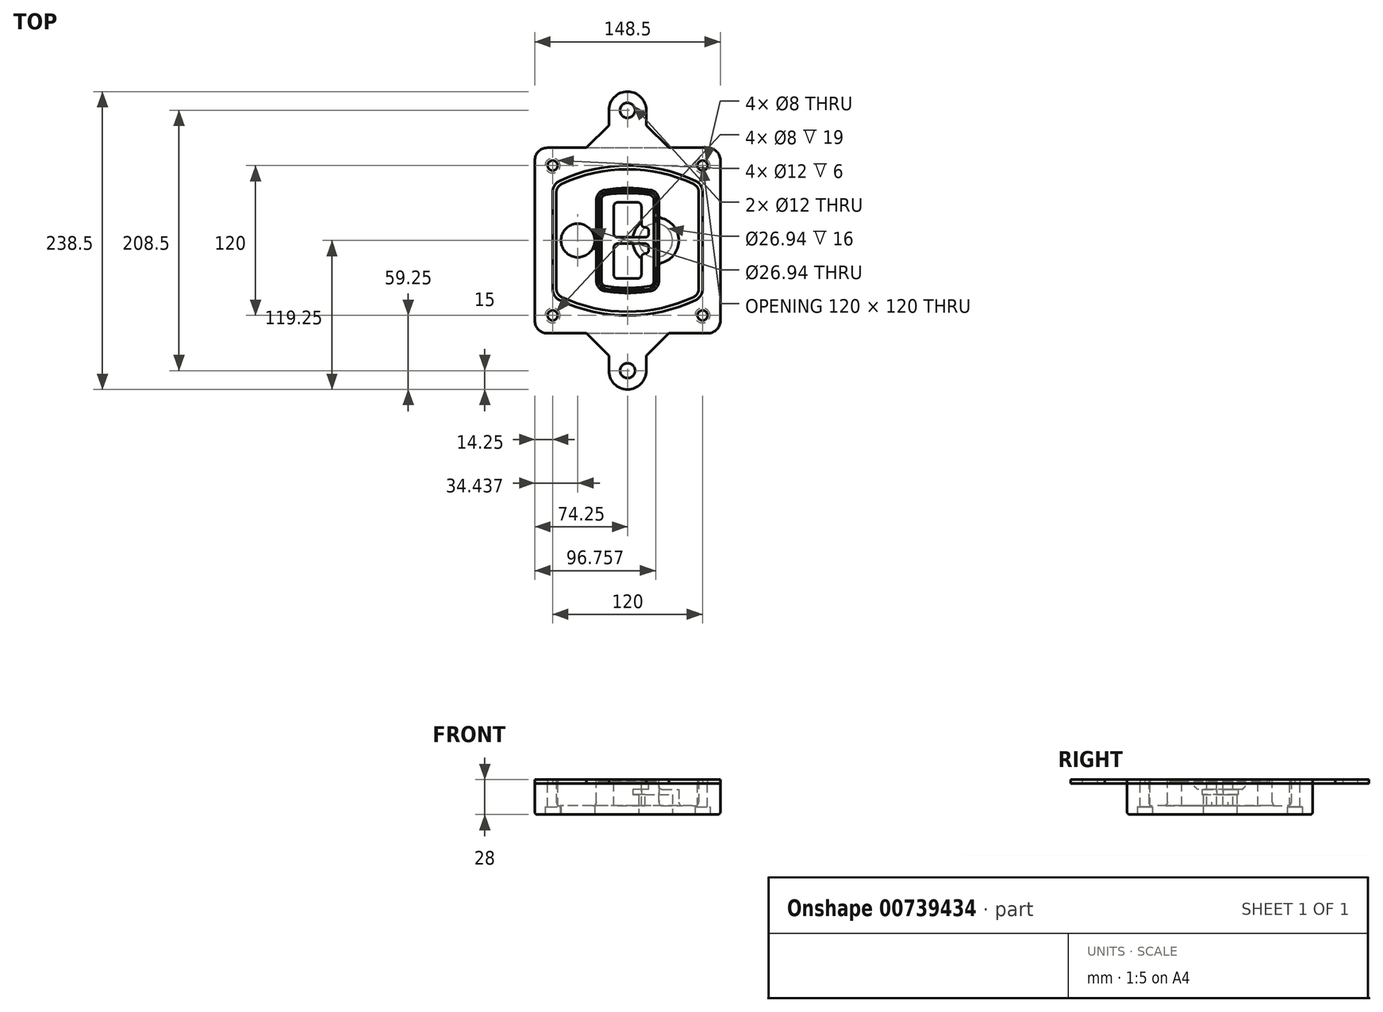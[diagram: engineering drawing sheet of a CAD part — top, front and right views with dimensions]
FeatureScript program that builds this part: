
annotation { "Feature Type Name" : "Feature", "Feature Type Description" : "" }
export const myFeature = defineFeature(function(context is Context, id is Id, definition is map)
    precondition{}
    {
        {
            var Q0;
            Q0=qCreatedBy(makeId("Top.planeOp"),FACE);
            var sketch = newSketch(context, id + "F0", { "sketchPlane" : qUnion([Q0])});
            skPoint(sketch, "E0.rect.middle", {"position": v(0, 0) * mm});
            skLineSegment(sketch, "E1.bottom", {"start": v(-64.25, -74.25) * mm, "end": v(64.25, -74.25) * mm});
            skLineSegment(sketch, "E1.top", {"start": v(-64.25, 74.25) * mm, "end": v(64.25, 74.25) * mm});
            skLineSegment(sketch, "E1.left", {"start": v(-74.25, -64.25) * mm, "end": v(-74.25, 64.25) * mm});
            skLineSegment(sketch, "E1.right", {"start": v(74.25, -64.25) * mm, "end": v(74.25, 64.25) * mm});
            skLineSegment(sketch, "E2", {"start": v(-74.25, 74.25) * mm, "end": v(74.25, -74.25) * mm, "construction": true});
            skLineSegment(sketch, "E3", {"start": v(74.25, 74.25) * mm, "end": v(-74.25, -74.25) * mm, "construction": true});
            skCircle(sketch, "E4", {"center": v(-60, 60) * mm, "radius": 4 * mm});
            skCircle(sketch, "E5", {"center": v(60, 60) * mm, "radius": 4 * mm});
            skCircle(sketch, "E6", {"center": v(60, -60) * mm, "radius": 4 * mm});
            skCircle(sketch, "E7", {"center": v(-60, -60) * mm, "radius": 4 * mm});
            skLineSegment(sketch, "E8", {"start": v(-60, 60) * mm, "end": v(60, 60) * mm, "construction": true});
            skLineSegment(sketch, "E9", {"start": v(60, 60) * mm, "end": v(60, -60) * mm, "construction": true});
            skLineSegment(sketch, "E10", {"start": v(60, -60) * mm, "end": v(-60, -60) * mm, "construction": true});
            skLineSegment(sketch, "E11", {"start": v(-60, -60) * mm, "end": v(-60, 60) * mm, "construction": true});
            skLineSegment(sketch, "E12", {"start": v(-60, 38.83) * mm, "end": v(-60, -38.83) * mm});
            skLineSegment(sketch, "E13", {"start": v(60, 38.83) * mm, "end": v(60, -38.83) * mm});
            skArc(sketch, "E14", {"start": v(54.26, 47.88) * mm, "mid": v(0, 60) * mm, "end": v(-54.26, 47.88) * mm});
            skArc(sketch, "E15", {"start": v(-54.26, -47.88) * mm, "mid": v(0, -60) * mm, "end": v(54.26, -47.88) * mm});
            skLineSegment(sketch, "E16", {"start": v(-60, 0) * mm, "end": v(60, 0) * mm, "construction": true});
            skPoint(sketch, "E17.visualSharp", {"position": v(-60, -45) * mm});
            skArc(sketch, "E17.filletArc", {"start": v(-60, -38.83) * mm, "mid": v(-58.44, -44.2) * mm, "end": v(-54.26, -47.88) * mm});
            skPoint(sketch, "E18.visualSharp", {"position": v(-60, 45) * mm});
            skArc(sketch, "E18.filletArc", {"start": v(-54.26, 47.88) * mm, "mid": v(-58.44, 44.2) * mm, "end": v(-60, 38.83) * mm});
            skPoint(sketch, "E19.visualSharp", {"position": v(60, 45) * mm});
            skArc(sketch, "E19.filletArc", {"start": v(60, 38.83) * mm, "mid": v(58.44, 44.2) * mm, "end": v(54.26, 47.88) * mm});
            skPoint(sketch, "E20.visualSharp", {"position": v(60, -45) * mm});
            skArc(sketch, "E20.filletArc", {"start": v(54.26, -47.88) * mm, "mid": v(58.44, -44.2) * mm, "end": v(60, -38.83) * mm});
            skPoint(sketch, "E21.visualSharp", {"position": v(-74.25, 74.25) * mm});
            skArc(sketch, "E21.filletArc", {"start": v(-64.25, 74.25) * mm, "mid": v(-71.32, 71.32) * mm, "end": v(-74.25, 64.25) * mm});
            skPoint(sketch, "E22.visualSharp", {"position": v(74.25, 74.25) * mm});
            skArc(sketch, "E22.filletArc", {"start": v(74.25, 64.25) * mm, "mid": v(71.32, 71.32) * mm, "end": v(64.25, 74.25) * mm});
            skPoint(sketch, "E23.visualSharp", {"position": v(74.25, -74.25) * mm});
            skArc(sketch, "E23.filletArc", {"start": v(64.25, -74.25) * mm, "mid": v(71.32, -71.32) * mm, "end": v(74.25, -64.25) * mm});
            skPoint(sketch, "E24.visualSharp", {"position": v(-74.25, -74.25) * mm});
            skArc(sketch, "E24.filletArc", {"start": v(-74.25, -64.25) * mm, "mid": v(-71.32, -71.32) * mm, "end": v(-64.25, -74.25) * mm});
            skArc(sketch, "E25.0", {"start": v(57, 38.83) * mm, "mid": v(55.9, 42.58) * mm, "end": v(52.98, 45.17) * mm});
            skLineSegment(sketch, "E25.1", {"start": v(57, 38.83) * mm, "end": v(57, -38.83) * mm});
            skArc(sketch, "E25.2", {"start": v(52.98, -45.17) * mm, "mid": v(55.9, -42.58) * mm, "end": v(57, -38.83) * mm});
            skArc(sketch, "E25.3", {"start": v(-52.98, -45.17) * mm, "mid": v(0, -57) * mm, "end": v(52.98, -45.17) * mm});
            skArc(sketch, "E25.4", {"start": v(-57, -38.83) * mm, "mid": v(-55.9, -42.58) * mm, "end": v(-52.98, -45.17) * mm});
            skArc(sketch, "E25.5", {"start": v(52.98, 45.17) * mm, "mid": v(0, 57) * mm, "end": v(-52.98, 45.17) * mm});
            skLineSegment(sketch, "E25.6", {"start": v(-57, 38.83) * mm, "end": v(-57, -38.83) * mm});
            skArc(sketch, "E25.7", {"start": v(-52.98, 45.17) * mm, "mid": v(-55.9, 42.58) * mm, "end": v(-57, 38.83) * mm});
            skArc(sketch, "E26.0", {"start": v(-55.96, 51.5) * mm, "mid": v(-61.82, 46.33) * mm, "end": v(-64, 38.83) * mm});
            skArc(sketch, "E26.1", {"start": v(55.96, 51.5) * mm, "mid": v(0, 64) * mm, "end": v(-55.96, 51.5) * mm});
            skArc(sketch, "E26.2", {"start": v(64, 38.83) * mm, "mid": v(61.82, 46.33) * mm, "end": v(55.96, 51.5) * mm});
            skLineSegment(sketch, "E26.3", {"start": v(64, 38.83) * mm, "end": v(64, -38.83) * mm});
            skArc(sketch, "E26.4", {"start": v(55.96, -51.5) * mm, "mid": v(61.82, -46.33) * mm, "end": v(64, -38.83) * mm});
            skLineSegment(sketch, "E26.5", {"start": v(-64, 38.83) * mm, "end": v(-64, -38.83) * mm});
            skArc(sketch, "E26.6", {"start": v(-55.96, -51.5) * mm, "mid": v(0, -64) * mm, "end": v(55.96, -51.5) * mm});
            skArc(sketch, "E26.7", {"start": v(-64, -38.83) * mm, "mid": v(-61.82, -46.33) * mm, "end": v(-55.96, -51.5) * mm});
            skSolve(sketch);
        }
        {
            var Q0;
            Q0=makeQuery(id+"F0.imprint","IMPRINT",FACE,{"disambiguationData":[TD([[makeQuery(id+"F0.imprint","IMPRINT",EDGE,{"derivedFrom":sQuery(id+"F0.wireOp",EDGE,"E1.bottom")}),1.0]])]});
            var Q1;
            Q1=makeQuery(id+"F0.imprint","IMPRINT",FACE,{"disambiguationData":[TD([[makeQuery(id+"F0.imprint","IMPRINT",EDGE,{"derivedFrom":sQuery(id+"F0.wireOp",EDGE,"E12")}),1.0]])]});
            var Q2;
            Q2=makeQuery(id+"F0.imprint","IMPRINT",FACE,{"disambiguationData":[TD([[makeQuery(id+"F0.imprint","IMPRINT",EDGE,{"derivedFrom":sQuery(id+"F0.wireOp",EDGE,"E25.0")}),1.0]])]});
            var Q3;
            Q3=makeQuery(id+"F0.imprint","IMPRINT",FACE,{"disambiguationData":[TD([[makeQuery(id+"F0.imprint","IMPRINT",EDGE,{"derivedFrom":sQuery(id+"F0.wireOp",EDGE,"E12")}),-1.0]])]});
            extrude(context, id + "F1", {"entities" : qUnion([Q0, Q1, Q2, Q3]), "oppositeDirection" : true, "depth" : 25 * mm});
        }
        {
            var Q0;
            Q0=makeQuery(id+"F0.imprint","IMPRINT",FACE,{"disambiguationData":[TD([[makeQuery(id+"F0.imprint","IMPRINT",EDGE,{"derivedFrom":sQuery(id+"F0.wireOp",EDGE,"E12")}),1.0]])]});
            extrude(context, id + "F2", {"entities" : qUnion([Q0]), "operationType" : NewBodyOperationType.ADD, "depth" : 3 * mm});
        }
        {
            var Q0;
            Q0=makeQuery(id+"F0.imprint","IMPRINT",FACE,{"disambiguationData":[TD([[makeQuery(id+"F0.imprint","IMPRINT",EDGE,{"derivedFrom":sQuery(id+"F0.wireOp",EDGE,"E25.0")}),1.0]])]});
            extrude(context, id + "F3", {"entities" : qUnion([Q0]), "operationType" : NewBodyOperationType.REMOVE, "oppositeDirection" : true, "depth" : 18 * mm});
        }
        {
            var Q0;
            Q0=makeQuery(id+"F2.opExtrude","CAP_FACE",FACE,{"disambiguationData":[OSD([sQuery(id+"F0.wireOp",EDGE,"E12"),sQuery(id+"F0.wireOp",EDGE,"E13"),sQuery(id+"F0.wireOp",EDGE,"E14"),sQuery(id+"F0.wireOp",EDGE,"E15"),sQuery(id+"F0.wireOp",EDGE,"E17.filletArc"),sQuery(id+"F0.wireOp",EDGE,"E18.filletArc"),sQuery(id+"F0.wireOp",EDGE,"E19.filletArc"),sQuery(id+"F0.wireOp",EDGE,"E20.filletArc"),sQuery(id+"F0.wireOp",EDGE,"E25.0"),sQuery(id+"F0.wireOp",EDGE,"E25.1"),sQuery(id+"F0.wireOp",EDGE,"E25.2"),sQuery(id+"F0.wireOp",EDGE,"E25.3"),sQuery(id+"F0.wireOp",EDGE,"E25.4"),sQuery(id+"F0.wireOp",EDGE,"E25.5"),sQuery(id+"F0.wireOp",EDGE,"E25.6"),sQuery(id+"F0.wireOp",EDGE,"E25.7")])],"isStart":false});
            var sketch = newSketch(context, id + "F4", { "sketchPlane" : qUnion([Q0])});
            skArc(sketch, "E27.0", {"start": v(-18.34, -40.45) * mm, "mid": v(0, -42) * mm, "end": v(18.34, -40.45) * mm});
            skArc(sketch, "E28.0", {"start": v(18.34, 40.45) * mm, "mid": v(0, 42) * mm, "end": v(-18.34, 40.45) * mm});
            skLineSegment(sketch, "E29", {"start": v(-25, 32.57) * mm, "end": v(-25, -32.57) * mm});
            skLineSegment(sketch, "E30", {"start": v(25, 32.57) * mm, "end": v(25, -32.57) * mm});
            skLineSegment(sketch, "E31", {"start": v(-25, 39.1) * mm, "end": v(25, 39.1) * mm, "construction": true});
            skLineSegment(sketch, "E32", {"start": v(-25, -39.1) * mm, "end": v(25, -39.1) * mm, "construction": true});
            skPoint(sketch, "E33.visualSharp", {"position": v(-25, 39.1) * mm});
            skArc(sketch, "E33.filletArc", {"start": v(-18.34, 40.45) * mm, "mid": v(-23.11, 37.73) * mm, "end": v(-25, 32.57) * mm});
            skPoint(sketch, "E34.visualSharp", {"position": v(25, 39.1) * mm});
            skArc(sketch, "E34.filletArc", {"start": v(25, 32.57) * mm, "mid": v(23.11, 37.73) * mm, "end": v(18.34, 40.45) * mm});
            skPoint(sketch, "E35.visualSharp", {"position": v(25, -39.1) * mm});
            skArc(sketch, "E35.filletArc", {"start": v(18.34, -40.45) * mm, "mid": v(23.11, -37.73) * mm, "end": v(25, -32.57) * mm});
            skPoint(sketch, "E36.visualSharp", {"position": v(-25, -39.1) * mm});
            skArc(sketch, "E36.filletArc", {"start": v(-25, -32.57) * mm, "mid": v(-23.11, -37.73) * mm, "end": v(-18.34, -40.45) * mm});
            skArc(sketch, "E37.0", {"start": v(52.98, 45.17) * mm, "mid": v(0, 57) * mm, "end": v(-52.98, 45.17) * mm});
            skArc(sketch, "E37.1", {"start": v(-52.98, 45.17) * mm, "mid": v(-55.9, 42.58) * mm, "end": v(-57, 38.83) * mm});
            skLineSegment(sketch, "E37.2", {"start": v(-57, 38.83) * mm, "end": v(-57, -38.83) * mm});
            skArc(sketch, "E37.3", {"start": v(-57, -38.83) * mm, "mid": v(-55.9, -42.58) * mm, "end": v(-52.98, -45.17) * mm});
            skArc(sketch, "E37.4", {"start": v(-52.98, -45.17) * mm, "mid": v(0, -57) * mm, "end": v(52.98, -45.17) * mm});
            skArc(sketch, "E37.5", {"start": v(52.98, -45.17) * mm, "mid": v(55.9, -42.58) * mm, "end": v(57, -38.83) * mm});
            skLineSegment(sketch, "E37.6", {"start": v(57, 38.83) * mm, "end": v(57, -38.83) * mm});
            skArc(sketch, "E37.7", {"start": v(57, 38.83) * mm, "mid": v(55.9, 42.58) * mm, "end": v(52.98, 45.17) * mm});
            skLineSegment(sketch, "E38.0", {"start": v(23, 32.57) * mm, "end": v(23, -32.57) * mm});
            skArc(sketch, "E38.1", {"start": v(18, -38.48) * mm, "mid": v(21.58, -36.44) * mm, "end": v(23, -32.57) * mm});
            skArc(sketch, "E38.2", {"start": v(-18, -38.48) * mm, "mid": v(0, -40) * mm, "end": v(18, -38.48) * mm});
            skArc(sketch, "E38.3", {"start": v(-23, -32.57) * mm, "mid": v(-21.58, -36.44) * mm, "end": v(-18, -38.48) * mm});
            skLineSegment(sketch, "E38.4", {"start": v(-23, 32.57) * mm, "end": v(-23, -32.57) * mm});
            skArc(sketch, "E38.5", {"start": v(23, 32.57) * mm, "mid": v(21.58, 36.44) * mm, "end": v(18, 38.48) * mm});
            skArc(sketch, "E38.6", {"start": v(-18, 38.48) * mm, "mid": v(-21.58, 36.44) * mm, "end": v(-23, 32.57) * mm});
            skArc(sketch, "E38.7", {"start": v(18, 38.48) * mm, "mid": v(0, 40) * mm, "end": v(-18, 38.48) * mm});
            skArc(sketch, "E39.0", {"start": v(21, 32.57) * mm, "mid": v(20.06, 35.15) * mm, "end": v(17.67, 36.5) * mm});
            skLineSegment(sketch, "E39.1", {"start": v(21, 32.57) * mm, "end": v(21, -32.57) * mm});
            skArc(sketch, "E39.2", {"start": v(17.67, -36.5) * mm, "mid": v(20.06, -35.15) * mm, "end": v(21, -32.57) * mm});
            skArc(sketch, "E39.3", {"start": v(-17.67, -36.5) * mm, "mid": v(0, -38) * mm, "end": v(17.67, -36.5) * mm});
            skArc(sketch, "E39.4", {"start": v(-21, -32.57) * mm, "mid": v(-20.06, -35.15) * mm, "end": v(-17.67, -36.5) * mm});
            skArc(sketch, "E39.5", {"start": v(17.67, 36.5) * mm, "mid": v(0, 38) * mm, "end": v(-17.67, 36.5) * mm});
            skLineSegment(sketch, "E39.6", {"start": v(-21, 32.57) * mm, "end": v(-21, -32.57) * mm});
            skArc(sketch, "E39.7", {"start": v(-17.67, 36.5) * mm, "mid": v(-20.06, 35.15) * mm, "end": v(-21, 32.57) * mm});
            skLineSegment(sketch, "E40", {"start": v(-25, 0) * mm, "end": v(25, 0) * mm, "construction": true});
            skLineSegment(sketch, "E41", {"start": v(-11, 5.5) * mm, "end": v(-11, 27.5) * mm});
            skLineSegment(sketch, "E42", {"start": v(-8, 30.5) * mm, "end": v(8, 30.5) * mm});
            skLineSegment(sketch, "E43", {"start": v(11, 27.5) * mm, "end": v(11, 13.5) * mm});
            skLineSegment(sketch, "E44", {"start": v(14, 10.5) * mm, "end": v(14, 10.5) * mm});
            skLineSegment(sketch, "E45", {"start": v(17, 7.5) * mm, "end": v(17, 5.5) * mm});
            skLineSegment(sketch, "E46", {"start": v(14, 2.5) * mm, "end": v(-8, 2.5) * mm});
            skPoint(sketch, "E47.visualSharp", {"position": v(-11, 30.5) * mm});
            skArc(sketch, "E47.filletArc", {"start": v(-8, 30.5) * mm, "mid": v(-10.12, 29.62) * mm, "end": v(-11, 27.5) * mm});
            skPoint(sketch, "E48.visualSharp", {"position": v(11, 30.5) * mm});
            skArc(sketch, "E48.filletArc", {"start": v(11, 27.5) * mm, "mid": v(10.12, 29.62) * mm, "end": v(8, 30.5) * mm});
            skPoint(sketch, "E49.visualSharp", {"position": v(11, 10.5) * mm});
            skArc(sketch, "E49.filletArc", {"start": v(11, 13.5) * mm, "mid": v(11.88, 11.38) * mm, "end": v(14, 10.5) * mm});
            skPoint(sketch, "E50.visualSharp", {"position": v(17, 10.5) * mm});
            skArc(sketch, "E50.filletArc", {"start": v(17, 7.5) * mm, "mid": v(16.12, 9.62) * mm, "end": v(14, 10.5) * mm});
            skPoint(sketch, "E51.visualSharp", {"position": v(17, 2.5) * mm});
            skArc(sketch, "E51.filletArc", {"start": v(14, 2.5) * mm, "mid": v(16.12, 3.38) * mm, "end": v(17, 5.5) * mm});
            skPoint(sketch, "E52.visualSharp", {"position": v(-11, 2.5) * mm});
            skArc(sketch, "E52.filletArc", {"start": v(-11, 5.5) * mm, "mid": v(-10.12, 3.38) * mm, "end": v(-8, 2.5) * mm});
            skLineSegment(sketch, "E53.0.MirrorCS", {"start": v(14, -2.5) * mm, "end": v(-8, -2.5) * mm});
            skArc(sketch, "E54.0.MirrorCS", {"start": v(-11, -5.5) * mm, "mid": v(-10.12, -3.38) * mm, "end": v(-8, -2.5) * mm});
            skLineSegment(sketch, "E55.0.MirrorCS", {"start": v(-11, -5.5) * mm, "end": v(-11, -27.5) * mm});
            skArc(sketch, "E56.0.MirrorCS", {"start": v(-8, -30.5) * mm, "mid": v(-10.12, -29.62) * mm, "end": v(-11, -27.5) * mm});
            skLineSegment(sketch, "E57.0.MirrorCS", {"start": v(-8, -30.5) * mm, "end": v(8, -30.5) * mm});
            skArc(sketch, "E58.0.MirrorCS", {"start": v(11, -27.5) * mm, "mid": v(10.12, -29.62) * mm, "end": v(8, -30.5) * mm});
            skLineSegment(sketch, "E59.0.MirrorCS", {"start": v(11, -27.5) * mm, "end": v(11, -13.5) * mm});
            skArc(sketch, "E60.0.MirrorCS", {"start": v(11, -13.5) * mm, "mid": v(11.88, -11.38) * mm, "end": v(14, -10.5) * mm});
            skArc(sketch, "E61.0.MirrorCS", {"start": v(17, -7.5) * mm, "mid": v(16.12, -9.62) * mm, "end": v(14, -10.5) * mm});
            skLineSegment(sketch, "E62.0.MirrorCS", {"start": v(17, -7.5) * mm, "end": v(17, -5.5) * mm});
            skArc(sketch, "E63.0.MirrorCS", {"start": v(14, -2.5) * mm, "mid": v(16.12, -3.38) * mm, "end": v(17, -5.5) * mm});
            skSolve(sketch);
        }
        {
            var Q0;
            Q0=makeQuery(id+"F4.imprint","IMPRINT",FACE,{"disambiguationData":[TD([[makeQuery(id+"F4.imprint","IMPRINT",EDGE,{"derivedFrom":sQuery(id+"F4.wireOp",EDGE,"E27.0")}),1.0]])]});
            var Q1;
            Q1=makeQuery(id+"F4.imprint","IMPRINT",FACE,{"disambiguationData":[TD([[makeQuery(id+"F4.imprint","IMPRINT",EDGE,{"derivedFrom":sQuery(id+"F4.wireOp",EDGE,"E38.0")}),-1.0]])]});
            var Q2;
            Q2=makeQuery(id+"F4.imprint","IMPRINT",FACE,{"disambiguationData":[TD([[makeQuery(id+"F4.imprint","IMPRINT",EDGE,{"derivedFrom":sQuery(id+"F4.wireOp",EDGE,"E39.0")}),1.0]])]});
            extrude(context, id + "F5", {"entities" : qUnion([Q0, Q1, Q2]), "operationType" : NewBodyOperationType.ADD, "endBound" : BoundingType.UP_TO_NEXT, "oppositeDirection" : true, "depth" : 25 * mm});
        }
        {
            var Q0;
            Q0=makeQuery(id+"F4.imprint","IMPRINT",FACE,{"disambiguationData":[TD([[makeQuery(id+"F4.imprint","IMPRINT",EDGE,{"derivedFrom":sQuery(id+"F4.wireOp",EDGE,"E38.0")}),-1.0]])]});
            extrude(context, id + "F6", {"entities" : qUnion([Q0]), "operationType" : NewBodyOperationType.REMOVE, "oppositeDirection" : true, "depth" : 2 * mm});
        }
        {
            var Q0;
            Q0=makeQuery(id+"F1.opExtrude","CAP_FACE",FACE,{"disambiguationData":[OSD([sQuery(id+"F0.wireOp",EDGE,"E1.bottom"),sQuery(id+"F0.wireOp",EDGE,"E1.top"),sQuery(id+"F0.wireOp",EDGE,"E1.left"),sQuery(id+"F0.wireOp",EDGE,"E1.right"),sQuery(id+"F0.wireOp",EDGE,"E4"),sQuery(id+"F0.wireOp",EDGE,"E5"),sQuery(id+"F0.wireOp",EDGE,"E6"),sQuery(id+"F0.wireOp",EDGE,"E7"),sQuery(id+"F0.wireOp",EDGE,"E21.filletArc"),sQuery(id+"F0.wireOp",EDGE,"E22.filletArc"),sQuery(id+"F0.wireOp",EDGE,"E23.filletArc"),sQuery(id+"F0.wireOp",EDGE,"E24.filletArc")])],"isStart":false});
            var sketch = newSketch(context, id + "F7", { "sketchPlane" : qUnion([Q0])});
            skCircle(sketch, "E64", {"center": v(22.5, 0) * mm, "radius": 13.47 * mm});
            skCircle(sketch, "E65", {"center": v(-39.81, 0) * mm, "radius": 13.47 * mm});
            skLineSegment(sketch, "E66", {"start": v(74.25, 0) * mm, "end": v(-74.25, 0) * mm});
            skCircle(sketch, "E67", {"center": v(22.5, 0) * mm, "radius": 18.47 * mm});
            skCircle(sketch, "E68", {"center": v(60, -60) * mm, "radius": 6 * mm});
            skCircle(sketch, "E69", {"center": v(-60, -60) * mm, "radius": 6 * mm});
            skCircle(sketch, "E70", {"center": v(-60, 60) * mm, "radius": 6 * mm});
            skCircle(sketch, "E71", {"center": v(60, 60) * mm, "radius": 6 * mm});
            skSolve(sketch);
        }
        {
            var Q0;
            {var subQ1=sQuery(id+"F7.wireOp",EDGE,"E66");var subQ4=sQuery(id+"F7.wireOp",EDGE,"E64");var subQ6=makeQuery(id+"F7.imprint","INTERSECT",VERTEX,{"disambiguationData":[OD(0.0)],"derivedFrom":[subQ4,subQ1]});Q0=makeQuery(id+"F7.imprint","IMPRINT",FACE,{"disambiguationData":[TD([[makeQuery(id+"F7.imprint","IMPRINT",EDGE,{"disambiguationData":[TD([[subQ6,-1.0]])],"derivedFrom":subQ4}),-1.0]])]});}
            var Q1;
            {var subQ0=sQuery(id+"F7.wireOp",EDGE,"E66");var subQ1=sQuery(id+"F7.wireOp",EDGE,"E64");var subQ3=makeQuery(id+"F7.imprint","INTERSECT",VERTEX,{"disambiguationData":[OD(0.0)],"derivedFrom":[subQ1,subQ0]});Q1=makeQuery(id+"F7.imprint","IMPRINT",FACE,{"disambiguationData":[TD([[makeQuery(id+"F7.imprint","IMPRINT",EDGE,{"disambiguationData":[TD([[subQ3,-1.0]])],"derivedFrom":subQ1}),1.0]])]});}
            var Q2;
            {var subQ0=sQuery(id+"F7.wireOp",EDGE,"E66");var subQ1=sQuery(id+"F7.wireOp",EDGE,"E64");var subQ3=makeQuery(id+"F7.imprint","INTERSECT",VERTEX,{"disambiguationData":[OD(0.0)],"derivedFrom":[subQ1,subQ0]});Q2=makeQuery(id+"F7.imprint","IMPRINT",FACE,{"disambiguationData":[TD([[makeQuery(id+"F7.imprint","IMPRINT",EDGE,{"disambiguationData":[TD([[subQ3,1.0]])],"derivedFrom":subQ1}),1.0]])]});}
            var Q3;
            {var subQ1=sQuery(id+"F7.wireOp",EDGE,"E66");var subQ4=sQuery(id+"F7.wireOp",EDGE,"E64");var subQ6=makeQuery(id+"F7.imprint","INTERSECT",VERTEX,{"disambiguationData":[OD(0.0)],"derivedFrom":[subQ4,subQ1]});Q3=makeQuery(id+"F7.imprint","IMPRINT",FACE,{"disambiguationData":[TD([[makeQuery(id+"F7.imprint","IMPRINT",EDGE,{"disambiguationData":[TD([[subQ6,1.0]])],"derivedFrom":subQ4}),-1.0]])]});}
            extrude(context, id + "F8", {"entities" : qUnion([Q0, Q1, Q2, Q3]), "operationType" : NewBodyOperationType.ADD, "oppositeDirection" : true, "depth" : 20 * mm});
        }
        {
            var Q0;
            {var subQ0=sQuery(id+"F7.wireOp",EDGE,"E66");var subQ1=sQuery(id+"F7.wireOp",EDGE,"E64");var subQ3=makeQuery(id+"F7.imprint","INTERSECT",VERTEX,{"disambiguationData":[OD(0.0)],"derivedFrom":[subQ1,subQ0]});Q0=makeQuery(id+"F7.imprint","IMPRINT",FACE,{"disambiguationData":[TD([[makeQuery(id+"F7.imprint","IMPRINT",EDGE,{"disambiguationData":[TD([[subQ3,-1.0]])],"derivedFrom":subQ1}),1.0]])]});}
            var Q1;
            {var subQ0=sQuery(id+"F7.wireOp",EDGE,"E66");var subQ1=sQuery(id+"F7.wireOp",EDGE,"E64");var subQ3=makeQuery(id+"F7.imprint","INTERSECT",VERTEX,{"disambiguationData":[OD(0.0)],"derivedFrom":[subQ1,subQ0]});Q1=makeQuery(id+"F7.imprint","IMPRINT",FACE,{"disambiguationData":[TD([[makeQuery(id+"F7.imprint","IMPRINT",EDGE,{"disambiguationData":[TD([[subQ3,1.0]])],"derivedFrom":subQ1}),1.0]])]});}
            extrude(context, id + "F9", {"entities" : qUnion([Q0, Q1]), "operationType" : NewBodyOperationType.REMOVE, "oppositeDirection" : true, "depth" : 16 * mm});
        }
        {
            var Q0;
            {var subQ0=sQuery(id+"F7.wireOp",EDGE,"E66");var subQ1=sQuery(id+"F7.wireOp",EDGE,"E65");var subQ3=makeQuery(id+"F7.imprint","INTERSECT",VERTEX,{"disambiguationData":[OD(0.0)],"derivedFrom":[subQ1,subQ0]});Q0=makeQuery(id+"F7.imprint","IMPRINT",FACE,{"disambiguationData":[TD([[makeQuery(id+"F7.imprint","IMPRINT",EDGE,{"disambiguationData":[TD([[subQ3,-1.0]])],"derivedFrom":subQ1}),1.0]])]});}
            var Q1;
            {var subQ0=sQuery(id+"F7.wireOp",EDGE,"E66");var subQ1=sQuery(id+"F7.wireOp",EDGE,"E65");var subQ3=makeQuery(id+"F7.imprint","INTERSECT",VERTEX,{"disambiguationData":[OD(0.0)],"derivedFrom":[subQ1,subQ0]});Q1=makeQuery(id+"F7.imprint","IMPRINT",FACE,{"disambiguationData":[TD([[makeQuery(id+"F7.imprint","IMPRINT",EDGE,{"disambiguationData":[TD([[subQ3,1.0]])],"derivedFrom":subQ1}),1.0]])]});}
            extrude(context, id + "F10", {"entities" : qUnion([Q0, Q1]), "operationType" : NewBodyOperationType.REMOVE, "oppositeDirection" : true, "depth" : 25 * mm});
        }
        {
            var Q0;
            Q0=makeQuery(id+"F7.imprint","IMPRINT",FACE,{"disambiguationData":[TD([[makeQuery(id+"F7.imprint","IMPRINT",EDGE,{"derivedFrom":sQuery(id+"F7.wireOp",EDGE,"E68")}),1.0]])]});
            var Q1;
            Q1=makeQuery(id+"F7.imprint","IMPRINT",FACE,{"disambiguationData":[TD([[makeQuery(id+"F7.imprint","IMPRINT",EDGE,{"derivedFrom":makeQuery(id+"F1.opExtrude","CAP_EDGE",EDGE,{"disambiguationData":[OSD([sQuery(id+"F0.wireOp",EDGE,"E5")])],"isStart":false})}),-1.0]])]});
            var Q2;
            Q2=makeQuery(id+"F7.imprint","IMPRINT",FACE,{"disambiguationData":[TD([[makeQuery(id+"F7.imprint","IMPRINT",EDGE,{"derivedFrom":sQuery(id+"F7.wireOp",EDGE,"E69")}),1.0]])]});
            var Q3;
            Q3=makeQuery(id+"F7.imprint","IMPRINT",FACE,{"disambiguationData":[TD([[makeQuery(id+"F7.imprint","IMPRINT",EDGE,{"derivedFrom":makeQuery(id+"F1.opExtrude","CAP_EDGE",EDGE,{"disambiguationData":[OSD([sQuery(id+"F0.wireOp",EDGE,"E4")])],"isStart":false})}),-1.0]])]});
            var Q4;
            Q4=makeQuery(id+"F7.imprint","IMPRINT",FACE,{"disambiguationData":[TD([[makeQuery(id+"F7.imprint","IMPRINT",EDGE,{"derivedFrom":sQuery(id+"F7.wireOp",EDGE,"E70")}),1.0]])]});
            var Q5;
            Q5=makeQuery(id+"F7.imprint","IMPRINT",FACE,{"disambiguationData":[TD([[makeQuery(id+"F7.imprint","IMPRINT",EDGE,{"derivedFrom":makeQuery(id+"F1.opExtrude","CAP_EDGE",EDGE,{"disambiguationData":[OSD([sQuery(id+"F0.wireOp",EDGE,"E7")])],"isStart":false})}),-1.0]])]});
            var Q6;
            Q6=makeQuery(id+"F7.imprint","IMPRINT",FACE,{"disambiguationData":[TD([[makeQuery(id+"F7.imprint","IMPRINT",EDGE,{"derivedFrom":sQuery(id+"F7.wireOp",EDGE,"E71")}),1.0]])]});
            var Q7;
            Q7=makeQuery(id+"F7.imprint","IMPRINT",FACE,{"disambiguationData":[TD([[makeQuery(id+"F7.imprint","IMPRINT",EDGE,{"derivedFrom":makeQuery(id+"F1.opExtrude","CAP_EDGE",EDGE,{"disambiguationData":[OSD([sQuery(id+"F0.wireOp",EDGE,"E6")])],"isStart":false})}),-1.0]])]});
            extrude(context, id + "F11", {"entities" : qUnion([Q0, Q1, Q2, Q3, Q4, Q5, Q6, Q7]), "operationType" : NewBodyOperationType.REMOVE, "oppositeDirection" : true, "depth" : 6 * mm});
        }
        {
            var Q0;
            Q0=makeQuery(id+"F9.boolean.opBoolean","COPY",FACE,{"derivedFrom":makeQuery(id+"F9.opExtrude","CAP_FACE",FACE,{"disambiguationData":[OSD([sQuery(id+"F7.wireOp",EDGE,"E64")])],"isStart":false})});
            var sketch = newSketch(context, id + "F12", { "sketchPlane" : qUnion([Q0])});
            skArc(sketch, "E72.0", {"start": v(11, 14.45) * mm, "mid": v(6.45, 9.13) * mm, "end": v(4.2, 2.5) * mm});
            skArc(sketch, "E72.1", {"start": v(4.2, -2.5) * mm, "mid": v(6.45, -9.13) * mm, "end": v(11, -14.45) * mm});
            skLineSegment(sketch, "E73", {"start": v(4.2, -2.5) * mm, "end": v(14, -2.5) * mm});
            skLineSegment(sketch, "E74.0", {"start": v(14, 2.5) * mm, "end": v(4.2, 2.5) * mm});
            skArc(sketch, "E74.1", {"start": v(14, 2.5) * mm, "mid": v(16.12, 3.38) * mm, "end": v(17, 5.5) * mm});
            skLineSegment(sketch, "E74.2", {"start": v(17, 7.5) * mm, "end": v(17, 5.5) * mm});
            skArc(sketch, "E74.3", {"start": v(17, 7.5) * mm, "mid": v(16.12, 9.62) * mm, "end": v(14, 10.5) * mm});
            skArc(sketch, "E74.4", {"start": v(11, 13.5) * mm, "mid": v(11.88, 11.38) * mm, "end": v(14, 10.5) * mm});
            skLineSegment(sketch, "E74.5", {"start": v(11, 14.45) * mm, "end": v(11, 13.5) * mm});
            skLineSegment(sketch, "E74.7", {"start": v(14, -2.5) * mm, "end": v(4.2, -2.5) * mm});
            skArc(sketch, "E74.8", {"start": v(14, -2.5) * mm, "mid": v(16.12, -3.38) * mm, "end": v(17, -5.5) * mm});
            skLineSegment(sketch, "E74.9", {"start": v(17, -7.5) * mm, "end": v(17, -5.5) * mm});
            skArc(sketch, "E74.10", {"start": v(17, -7.5) * mm, "mid": v(16.12, -9.62) * mm, "end": v(14, -10.5) * mm});
            skArc(sketch, "E74.11", {"start": v(11, -13.5) * mm, "mid": v(11.88, -11.38) * mm, "end": v(14, -10.5) * mm});
            skLineSegment(sketch, "E74.12", {"start": v(11, -14.45) * mm, "end": v(11, -13.5) * mm});
            skPoint(sketch, "E75.orphan", {"position": v(11, -27.5) * mm});
            skPoint(sketch, "E76.orphan", {"position": v(-8, -2.5) * mm});
            skPoint(sketch, "E77.orphan", {"position": v(-8, 2.5) * mm});
            skPoint(sketch, "E78.orphan", {"position": v(11, 27.5) * mm});
            skSolve(sketch);
        }
        {
            var Q0;
            {var subQ7=sQuery(id+"F12.wireOp",EDGE,"E72.0");var subQ14=sQuery(id+"F12.wireOp",EDGE,"E72.1");var subQ16=sQuery(id+"F12.wireOp",EDGE,"E74.1");var subQ18=sQuery(id+"F12.wireOp",EDGE,"E74.8");Q0=qUnion([makeQuery(id+"F12.imprint","IMPRINT",FACE,{"disambiguationData":[TD([[makeQuery(id+"F12.imprint","IMPRINT",EDGE,{"derivedFrom":subQ7}),1.0]])]}),makeQuery(id+"F12.imprint","IMPRINT",FACE,{"disambiguationData":[TD([[makeQuery(id+"F12.imprint","IMPRINT",EDGE,{"derivedFrom":subQ14}),1.0]])]}),makeQuery(id+"F12.imprint","IMPRINT",FACE,{"disambiguationData":[TD([[makeQuery(id+"F12.imprint","IMPRINT",EDGE,{"derivedFrom":subQ16}),1.0]])]}),makeQuery(id+"F12.imprint","IMPRINT",FACE,{"disambiguationData":[TD([[makeQuery(id+"F12.imprint","IMPRINT",EDGE,{"derivedFrom":subQ18}),-1.0]])]})]);}
            var Q1;
            Q1=makeQuery(id+"F5.boolean.opBoolean","SPLIT",FACE,{"disambiguationData":[TD([makeQuery(id+"F5.opExtrude","SWEPT_FACE",FACE,{"disambiguationData":[OSD([sQuery(id+"F4.wireOp",EDGE,"E41")])]})])],"derivedFrom":makeQuery(id+"F3.boolean.opBoolean","COPY",FACE,{"derivedFrom":makeQuery(id+"F3.opExtrude","CAP_FACE",FACE,{"disambiguationData":[OSD([sQuery(id+"F0.wireOp",EDGE,"E25.0"),sQuery(id+"F0.wireOp",EDGE,"E25.1"),sQuery(id+"F0.wireOp",EDGE,"E25.2"),sQuery(id+"F0.wireOp",EDGE,"E25.3"),sQuery(id+"F0.wireOp",EDGE,"E25.4"),sQuery(id+"F0.wireOp",EDGE,"E25.5"),sQuery(id+"F0.wireOp",EDGE,"E25.6"),sQuery(id+"F0.wireOp",EDGE,"E25.7")])],"isStart":false})})});
            extrude(context, id + "F13", {"entities" : qUnion([Q0]), "operationType" : NewBodyOperationType.REMOVE, "endBound" : BoundingType.UP_TO_SURFACE, "endBoundEntityFace" : qUnion([Q1]), "depth" : 25 * mm});
        }
        {
            var Q0;
            Q0=makeQuery(id+"F3.boolean.opBoolean","COPY",EDGE,{"derivedFrom":makeQuery(id+"F3.opExtrude","CAP_EDGE",EDGE,{"disambiguationData":[OSD([sQuery(id+"F0.wireOp",EDGE,"E25.6")])],"isStart":false})});
            var Q1;
            Q1=makeQuery(id+"F8.boolean.opBoolean","INTERSECT",EDGE,{"derivedFrom":[makeQuery(id+"F5.opExtrude","SWEPT_FACE",FACE,{"disambiguationData":[OSD([sQuery(id+"F4.wireOp",EDGE,"E30")])]}),makeQuery(id+"F8.opExtrude","CAP_FACE",FACE,{"disambiguationData":[OSD([sQuery(id+"F7.wireOp",EDGE,"E67")])],"isStart":false})]});
            var Q2;
            Q2=makeQuery(id+"F8.boolean.opBoolean","INTERSECT",EDGE,{"disambiguationData":[OD(1.0)],"derivedFrom":[makeQuery(id+"F5.opExtrude","SWEPT_FACE",FACE,{"disambiguationData":[OSD([sQuery(id+"F4.wireOp",EDGE,"E30")])]}),makeQuery(id+"F8.opExtrude","SWEPT_FACE",FACE,{"disambiguationData":[OSD([sQuery(id+"F7.wireOp",EDGE,"E67")])]})]});
            var Q3;
            {var subQ0=sQuery(id+"F4.wireOp",EDGE,"E30");Q3=makeQuery(id+"F8.boolean.opBoolean","SPLIT",EDGE,{"disambiguationData":[TD([makeQuery(id+"F5.opExtrude","SWEPT_FACE",FACE,{"disambiguationData":[OSD([sQuery(id+"F4.wireOp",EDGE,"E35.filletArc")])]})])],"derivedFrom":makeQuery(id+"F5.opExtrude","CAP_EDGE",EDGE,{"disambiguationData":[OSD([subQ0])],"isStart":false})});}
            var Q4;
            {var subQ0=sQuery(id+"F0.wireOp",EDGE,"E25.7");var subQ1=sQuery(id+"F0.wireOp",EDGE,"E25.1");var subQ2=sQuery(id+"F0.wireOp",EDGE,"E25.6");var subQ3=sQuery(id+"F0.wireOp",EDGE,"E25.5");var subQ4=sQuery(id+"F0.wireOp",EDGE,"E25.4");var subQ5=sQuery(id+"F0.wireOp",EDGE,"E25.0");var subQ6=sQuery(id+"F0.wireOp",EDGE,"E25.2");var subQ7=sQuery(id+"F0.wireOp",EDGE,"E25.3");Q4=makeQuery(id+"F8.boolean.opBoolean","INTERSECT",EDGE,{"derivedFrom":[makeQuery(id+"F5.boolean.opBoolean","SPLIT",FACE,{"disambiguationData":[TD([makeQuery(id+"F2.opExtrude","SWEPT_FACE",FACE,{"disambiguationData":[OSD([subQ5])]})])],"derivedFrom":makeQuery(id+"F3.boolean.opBoolean","COPY",FACE,{"derivedFrom":makeQuery(id+"F3.opExtrude","CAP_FACE",FACE,{"disambiguationData":[OSD([subQ5,subQ1,subQ6,subQ7,subQ4,subQ3,subQ2,subQ0])],"isStart":false})})}),makeQuery(id+"F8.opExtrude","SWEPT_FACE",FACE,{"disambiguationData":[OSD([sQuery(id+"F7.wireOp",EDGE,"E67")])]})]});}
            var Q5;
            Q5=makeQuery(id+"F8.boolean.opBoolean","INTERSECT",EDGE,{"disambiguationData":[OD(0.0)],"derivedFrom":[makeQuery(id+"F5.opExtrude","SWEPT_FACE",FACE,{"disambiguationData":[OSD([sQuery(id+"F4.wireOp",EDGE,"E30")])]}),makeQuery(id+"F8.opExtrude","SWEPT_FACE",FACE,{"disambiguationData":[OSD([sQuery(id+"F7.wireOp",EDGE,"E67")])]})]});
            fillet(context, id + "F14", {"entities" : qUnion([Q0, Q1, Q2, Q3, Q4, Q5]), "radius" : 3 * mm, "tangentPropagation" : true, "allowEdgeOverflow" : false});
        }
        {
            var Q0;
            Q0=makeQuery(id+"F1.opExtrude","CAP_EDGE",EDGE,{"disambiguationData":[OSD([sQuery(id+"F0.wireOp",EDGE,"E1.bottom")])],"isStart":false});
            fillet(context, id + "F15", {"entities" : qUnion([Q0]), "radius" : 2 * mm, "tangentPropagation" : true, "allowEdgeOverflow" : false});
        }
        {
            var Q0;
            {var subQ0=sQuery(id+"F0.wireOp",EDGE,"E21.filletArc");var subQ1=sQuery(id+"F0.wireOp",EDGE,"E7");var subQ2=sQuery(id+"F0.wireOp",EDGE,"E6");var subQ3=sQuery(id+"F0.wireOp",EDGE,"E5");var subQ4=sQuery(id+"F0.wireOp",EDGE,"E4");var subQ5=sQuery(id+"F0.wireOp",EDGE,"E22.filletArc");var subQ6=sQuery(id+"F0.wireOp",EDGE,"E1.bottom");var subQ7=sQuery(id+"F0.wireOp",EDGE,"E1.right");var subQ8=sQuery(id+"F0.wireOp",EDGE,"E1.top");var subQ9=sQuery(id+"F0.wireOp",EDGE,"E1.left");var subQ10=sQuery(id+"F0.wireOp",EDGE,"E23.filletArc");var subQ11=sQuery(id+"F0.wireOp",EDGE,"E24.filletArc");Q0=makeQuery(id+"F2.boolean.opBoolean","SPLIT",FACE,{"disambiguationData":[TD([makeQuery(id+"F1.opExtrude","SWEPT_FACE",FACE,{"disambiguationData":[OSD([subQ6])]})])],"derivedFrom":makeQuery(id+"F1.opExtrude","CAP_FACE",FACE,{"disambiguationData":[OSD([subQ6,subQ8,subQ9,subQ7,subQ4,subQ3,subQ2,subQ1,subQ0,subQ5,subQ10,subQ11])],"isStart":true})});}
            var sketch = newSketch(context, id + "F16", { "sketchPlane" : qUnion([Q0])});
            skLineSegment(sketch, "E79", {"start": v(-33, 74.25) * mm, "end": v(-15, 92.25) * mm});
            skLineSegment(sketch, "E80", {"start": v(-15, 92.25) * mm, "end": v(-15, 104.25) * mm});
            skLineSegment(sketch, "E81", {"start": v(33, 74.25) * mm, "end": v(15, 92.25) * mm});
            skLineSegment(sketch, "E82", {"start": v(15, 92.25) * mm, "end": v(15, 104.25) * mm});
            skCircle(sketch, "E83", {"center": v(0, 104.25) * mm, "radius": 6 * mm});
            skArc(sketch, "E84", {"start": v(15, 104.25) * mm, "mid": v(0, 119.25) * mm, "end": v(-15, 104.25) * mm});
            skLineSegment(sketch, "E85", {"start": v(0, 104.25) * mm, "end": v(0, 74.25) * mm, "construction": true});
            skLineSegment(sketch, "E86", {"start": v(74.25, 0) * mm, "end": v(-74.25, 0) * mm, "construction": true});
            skLineSegment(sketch, "E87.MirrorCS", {"start": v(15, -92.25) * mm, "end": v(15, -104.25) * mm});
            skLineSegment(sketch, "E88.MirrorCS", {"start": v(-15, -92.25) * mm, "end": v(-15, -104.25) * mm});
            skLineSegment(sketch, "E89.MirrorCS", {"start": v(0, -104.25) * mm, "end": v(0, -74.25) * mm, "construction": true});
            skArc(sketch, "E90.MirrorCS", {"start": v(15, -104.25) * mm, "mid": v(0, -119.25) * mm, "end": v(-15, -104.25) * mm});
            skCircle(sketch, "E91.MirrorC", {"center": v(0, -104.25) * mm, "radius": 6 * mm});
            skLineSegment(sketch, "E92.MirrorCS", {"start": v(-33, -74.25) * mm, "end": v(-15, -92.25) * mm});
            skLineSegment(sketch, "E93.MirrorCS", {"start": v(33, -74.25) * mm, "end": v(15, -92.25) * mm});
            skSolve(sketch);
        }
        {
            var Q0;
            {var subQ1=sQuery(id+"F16.wireOp",EDGE,"E79");Q0=makeQuery(id+"F16.imprint","IMPRINT",FACE,{"disambiguationData":[TD([[makeQuery(id+"F16.imprint","IMPRINT",EDGE,{"derivedFrom":subQ1}),-1.0]])]});}
            var Q1;
            Q1=makeQuery(id+"F16.imprint","IMPRINT",FACE,{"disambiguationData":[TD([[makeQuery(id+"F16.imprint","IMPRINT",EDGE,{"derivedFrom":makeQuery(id+"F1.opExtrude","CAP_EDGE",EDGE,{"disambiguationData":[OSD([sQuery(id+"F0.wireOp",EDGE,"E1.left")])],"isStart":true})}),-1.0]])]});
            var Q2;
            {var subQ1=sQuery(id+"F16.wireOp",EDGE,"E92.MirrorCS");Q2=makeQuery(id+"F16.imprint","IMPRINT",FACE,{"disambiguationData":[TD([[makeQuery(id+"F16.imprint","IMPRINT",EDGE,{"derivedFrom":subQ1}),1.0]])]});}
            var Q3;
            Q3=makeQuery(id+"F2.opExtrude","CAP_FACE",FACE,{"disambiguationData":[OSD([sQuery(id+"F0.wireOp",EDGE,"E12"),sQuery(id+"F0.wireOp",EDGE,"E13"),sQuery(id+"F0.wireOp",EDGE,"E14"),sQuery(id+"F0.wireOp",EDGE,"E15"),sQuery(id+"F0.wireOp",EDGE,"E17.filletArc"),sQuery(id+"F0.wireOp",EDGE,"E18.filletArc"),sQuery(id+"F0.wireOp",EDGE,"E19.filletArc"),sQuery(id+"F0.wireOp",EDGE,"E20.filletArc"),sQuery(id+"F0.wireOp",EDGE,"E25.0"),sQuery(id+"F0.wireOp",EDGE,"E25.1"),sQuery(id+"F0.wireOp",EDGE,"E25.2"),sQuery(id+"F0.wireOp",EDGE,"E25.3"),sQuery(id+"F0.wireOp",EDGE,"E25.4"),sQuery(id+"F0.wireOp",EDGE,"E25.5"),sQuery(id+"F0.wireOp",EDGE,"E25.6"),sQuery(id+"F0.wireOp",EDGE,"E25.7")])],"isStart":false});
            extrude(context, id + "F17", {"entities" : qUnion([Q0, Q1, Q2]), "endBound" : BoundingType.UP_TO_SURFACE, "depth" : 25 * mm, "endBoundEntityFace" : qUnion([Q3]), "offsetDistance" : 25 * mm});
        }
    });
